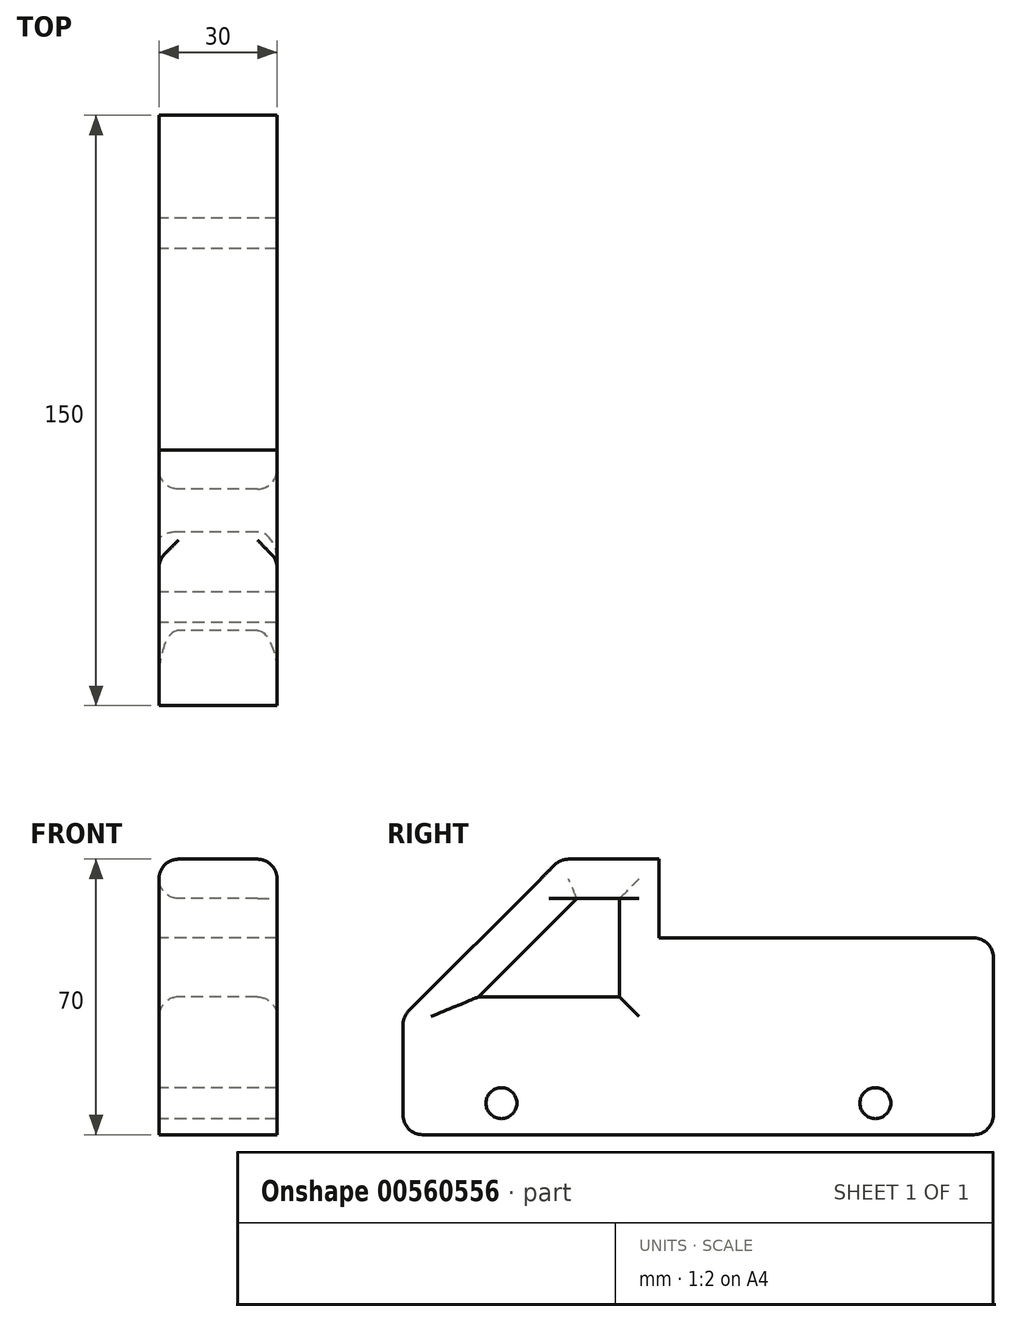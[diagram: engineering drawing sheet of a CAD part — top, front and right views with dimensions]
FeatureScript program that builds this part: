
annotation { "Feature Type Name" : "Feature", "Feature Type Description" : "" }
export const myFeature = defineFeature(function(context is Context, id is Id, definition is map)
    precondition{}
    {
        {
            var Q0;
            Q0=qCreatedBy(makeId("Right.planeOp"),FACE);
            var sketch = newSketch(context, id + "F0", { "sketchPlane" : qUnion([Q0])});
            skLineSegment(sketch, "E0", {"start": v(0, 0) * mm, "end": v(0, 30) * mm});
            skLineSegment(sketch, "E1", {"start": v(0, 30) * mm, "end": v(40, 70) * mm});
            skLineSegment(sketch, "E2", {"start": v(40, 70) * mm, "end": v(65, 70) * mm});
            skLineSegment(sketch, "E3", {"start": v(65, 70) * mm, "end": v(65, 50) * mm});
            skLineSegment(sketch, "E4", {"start": v(65, 50) * mm, "end": v(150, 50) * mm});
            skLineSegment(sketch, "E5", {"start": v(150, 50) * mm, "end": v(150, 0) * mm});
            skLineSegment(sketch, "E6", {"start": v(150, 0) * mm, "end": v(0, 0) * mm});
            skLineSegment(sketch, "E7.0", {"start": v(55, 60) * mm, "end": v(55, 35) * mm});
            skLineSegment(sketch, "E7.1", {"start": v(44.14, 60) * mm, "end": v(55, 60) * mm});
            skLineSegment(sketch, "E7.2", {"start": v(19.14, 35) * mm, "end": v(44.14, 60) * mm});
            skLineSegment(sketch, "E8", {"start": v(19.14, 35) * mm, "end": v(55, 35) * mm});
            skCircle(sketch, "E9", {"center": v(25, 8) * mm, "radius": 3.92 * mm});
            skCircle(sketch, "E10", {"center": v(120, 8) * mm, "radius": 3.92 * mm});
            skSolve(sketch);
        }
        {
            var Q0;
            Q0 = qSketchRegion(id + "F0", true);
            extrude(context, id + "F1", {"entities" : qUnion([Q0]), "endBound" : BoundingType.SYMMETRIC, "depth" : 30 * mm, "offsetDistance" : 25 * mm});
        }
        {
            var Q0;
            Q0=makeQuery(id+"F1.opExtrude","CAP_EDGE",EDGE,{"disambiguationData":[OSD([sQuery(id+"F0.wireOp",EDGE,"E2")])],"isStart":false});
            var Q1;
            Q1=makeQuery(id+"F1.opExtrude","SWEPT_EDGE",EDGE,{"disambiguationData":[OSD([sQuery(id+"F0.wireOp",EDGE,"E0"),sQuery(id+"F0.wireOp",EDGE,"E1")])]});
            var Q2;
            Q2=makeQuery(id+"F1.opExtrude","SWEPT_EDGE",EDGE,{"disambiguationData":[OSD([sQuery(id+"F0.wireOp",EDGE,"E0"),sQuery(id+"F0.wireOp",EDGE,"E6")])]});
            var Q3;
            Q3=makeQuery(id+"F1.opExtrude","SWEPT_EDGE",EDGE,{"disambiguationData":[OSD([sQuery(id+"F0.wireOp",EDGE,"E4"),sQuery(id+"F0.wireOp",EDGE,"E5")])]});
            var Q4;
            Q4=makeQuery(id+"F1.opExtrude","SWEPT_EDGE",EDGE,{"disambiguationData":[OSD([sQuery(id+"F0.wireOp",EDGE,"E1"),sQuery(id+"F0.wireOp",EDGE,"E2")])]});
            var Q5;
            Q5=makeQuery(id+"F1.opExtrude","CAP_EDGE",EDGE,{"disambiguationData":[OSD([sQuery(id+"F0.wireOp",EDGE,"E2")])],"isStart":true});
            var Q6;
            Q6=makeQuery(id+"F1.opExtrude","CAP_EDGE",EDGE,{"disambiguationData":[OSD([sQuery(id+"F0.wireOp",EDGE,"E8")])],"isStart":true});
            var Q7;
            Q7=makeQuery(id+"F1.opExtrude","CAP_EDGE",EDGE,{"disambiguationData":[OSD([sQuery(id+"F0.wireOp",EDGE,"E8")])],"isStart":false});
            var Q8;
            Q8=makeQuery(id+"F1.opExtrude","CAP_EDGE",EDGE,{"disambiguationData":[OSD([sQuery(id+"F0.wireOp",EDGE,"E7.0")])],"isStart":true});
            var Q9;
            Q9=makeQuery(id+"F1.opExtrude","CAP_EDGE",EDGE,{"disambiguationData":[OSD([sQuery(id+"F0.wireOp",EDGE,"E7.0")])],"isStart":false});
            var Q10;
            Q10=makeQuery(id+"F1.opExtrude","CAP_EDGE",EDGE,{"disambiguationData":[OSD([sQuery(id+"F0.wireOp",EDGE,"E7.2")])],"isStart":false});
            var Q11;
            Q11=makeQuery(id+"F1.opExtrude","CAP_EDGE",EDGE,{"disambiguationData":[OSD([sQuery(id+"F0.wireOp",EDGE,"E7.1")])],"isStart":true});
            var Q12;
            Q12=makeQuery(id+"F1.opExtrude","CAP_EDGE",EDGE,{"disambiguationData":[OSD([sQuery(id+"F0.wireOp",EDGE,"E7.2")])],"isStart":true});
            var Q13;
            Q13=makeQuery(id+"F1.opExtrude","SWEPT_EDGE",EDGE,{"disambiguationData":[OSD([sQuery(id+"F0.wireOp",EDGE,"E5"),sQuery(id+"F0.wireOp",EDGE,"E6")])]});
            fillet(context, id + "F2", {"entities" : qUnion([Q0, Q1, Q2, Q3, Q4, Q5, Q6, Q7, Q8, Q9, Q10, Q11, Q12, Q13]), "radius" : 5 * mm, "tangentPropagation" : true, "allowEdgeOverflow" : false});
        }
    });
